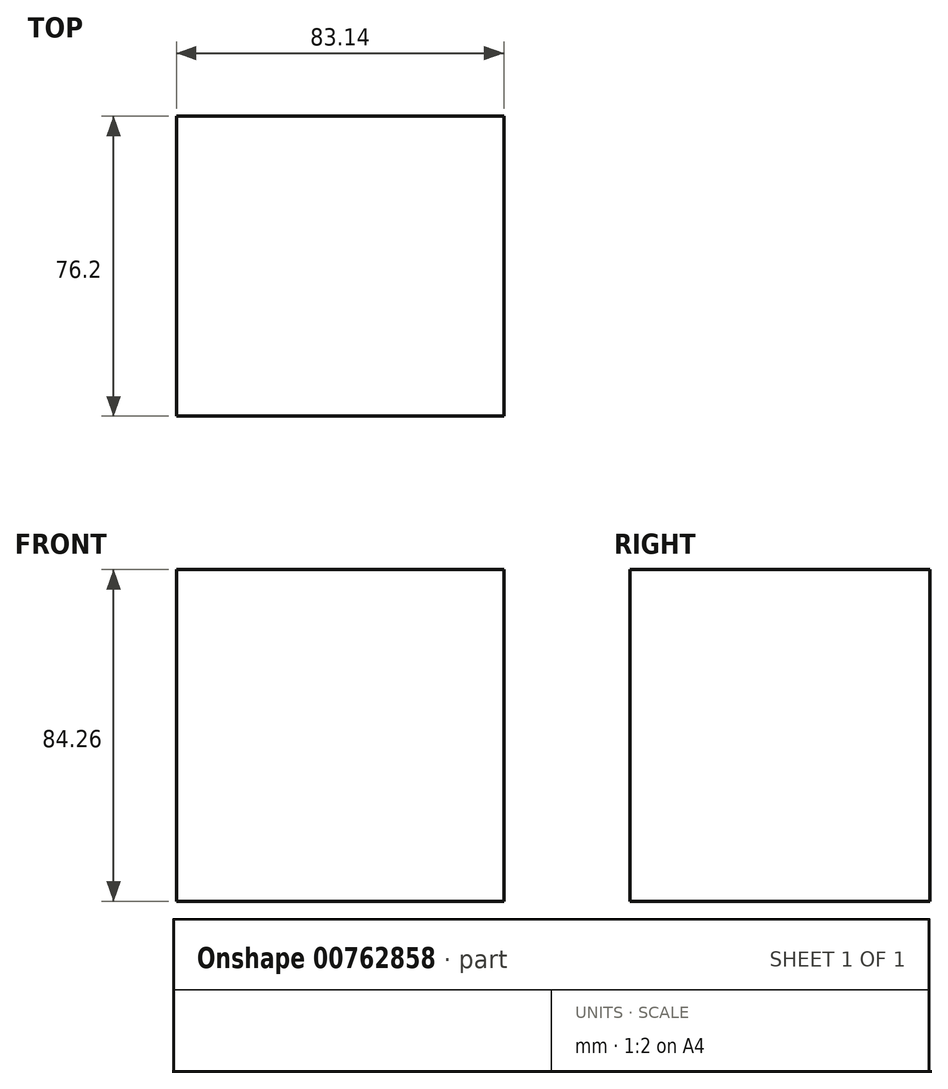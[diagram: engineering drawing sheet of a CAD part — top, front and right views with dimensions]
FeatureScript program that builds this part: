
annotation { "Feature Type Name" : "Feature", "Feature Type Description" : "" }
export const myFeature = defineFeature(function(context is Context, id is Id, definition is map)
    precondition{}
    {
        {
            var Q0;
            Q0=qCreatedBy(makeId("Front.planeOp"),FACE);
            var sketch = newSketch(context, id + "F0", { "sketchPlane" : qUnion([Q0])});
            skLineSegment(sketch, "E0.bottom", {"start": v(-57.5, 20.55) * mm, "end": v(25.65, 20.55) * mm});
            skLineSegment(sketch, "E0.top", {"start": v(-57.5, -63.7) * mm, "end": v(25.65, -63.7) * mm});
            skLineSegment(sketch, "E0.left", {"start": v(-57.5, 20.55) * mm, "end": v(-57.5, -63.7) * mm});
            skLineSegment(sketch, "E0.right", {"start": v(25.65, 20.55) * mm, "end": v(25.65, -63.7) * mm});
            skSolve(sketch);
        }
        {
            var Q0;
            Q0 = qSketchRegion(id + "F0", true);
            extrude(context, id + "F1", {"entities" : qUnion([Q0]), "depth" : 76.2 * mm, "offsetDistance" : 25.4 * mm});
        }
    });
